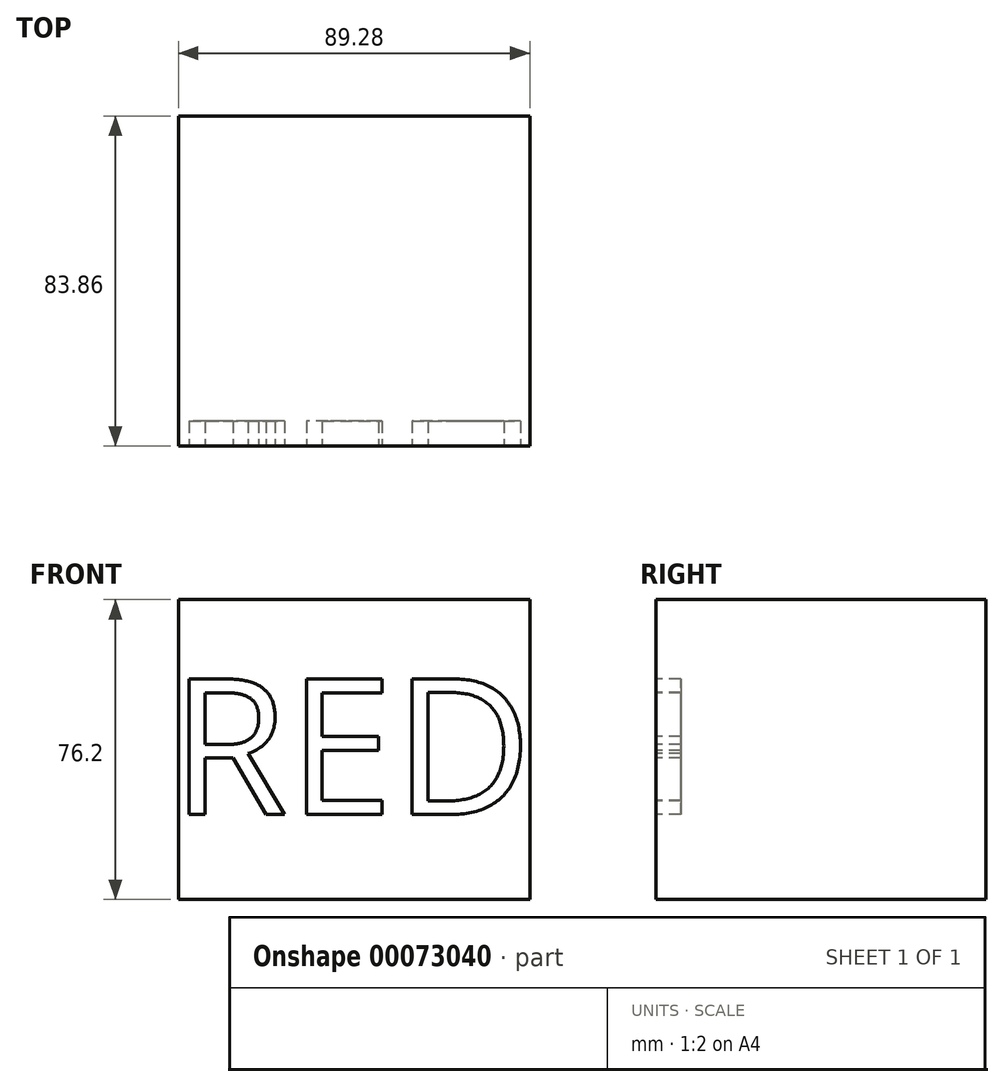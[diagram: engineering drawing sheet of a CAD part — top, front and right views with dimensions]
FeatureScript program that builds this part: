
annotation { "Feature Type Name" : "Feature", "Feature Type Description" : "" }
export const myFeature = defineFeature(function(context is Context, id is Id, definition is map)
    precondition{}
    {
        {
            var Q0;
            Q0=qCreatedBy(makeId("Top.planeOp"),FACE);
            var sketch = newSketch(context, id + "F0", { "sketchPlane" : qUnion([Q0])});
            skLineSegment(sketch, "E0.bottom", {"start": v(-44.5, 41.22) * mm, "end": v(44.78, 41.22) * mm});
            skLineSegment(sketch, "E0.top", {"start": v(-44.5, -42.64) * mm, "end": v(44.78, -42.64) * mm});
            skLineSegment(sketch, "E0.left", {"start": v(-44.5, 41.22) * mm, "end": v(-44.5, -42.64) * mm});
            skLineSegment(sketch, "E0.right", {"start": v(44.78, 41.22) * mm, "end": v(44.78, -42.64) * mm});
            skSolve(sketch);
        }
        {
            var Q0;
            Q0 = qSketchRegion(id + "F0", true);
            var Q1;
            Q1=makeQuery(id+"F0.imprint","IMPRINT",FACE,{"disambiguationData":[TD([[makeQuery(id+"F0.imprint","IMPRINT",EDGE,{"derivedFrom":sQuery(id+"F0.wireOp",EDGE,"E0.bottom")}),-1.0]])]});
            extrude(context, id + "F1", {"entities" : qUnion([Q0, Q1]), "depth" : 76.2 * mm});
        }
        {
            var Q0;
            Q0=makeQuery(id+"F1.opExtrude","SWEPT_FACE",FACE,{"disambiguationData":[OSD([sQuery(id+"F0.wireOp",EDGE,"E0.top")])]});
            var sketch = newSketch(context, id + "F2", { "sketchPlane" : qUnion([Q0])});
            skText(sketch, "E1", { "text": "RED", "fontName": "OpenSans-Regular.ttf"});
            const initialGuessF2  = {"E1": [-0.04651, 0.02159, 1, 0, 0.03475]};
            skSetInitialGuess(sketch, initialGuessF2);
            skSolve(sketch);
        }
        {
            var Q0;
            Q0 = qSketchRegion(id + "F2", true);
            extrude(context, id + "F3", {"entities" : qUnion([Q0]), "operationType" : NewBodyOperationType.REMOVE, "oppositeDirection" : true, "depth" : 6.35 * mm});
        }
    });
